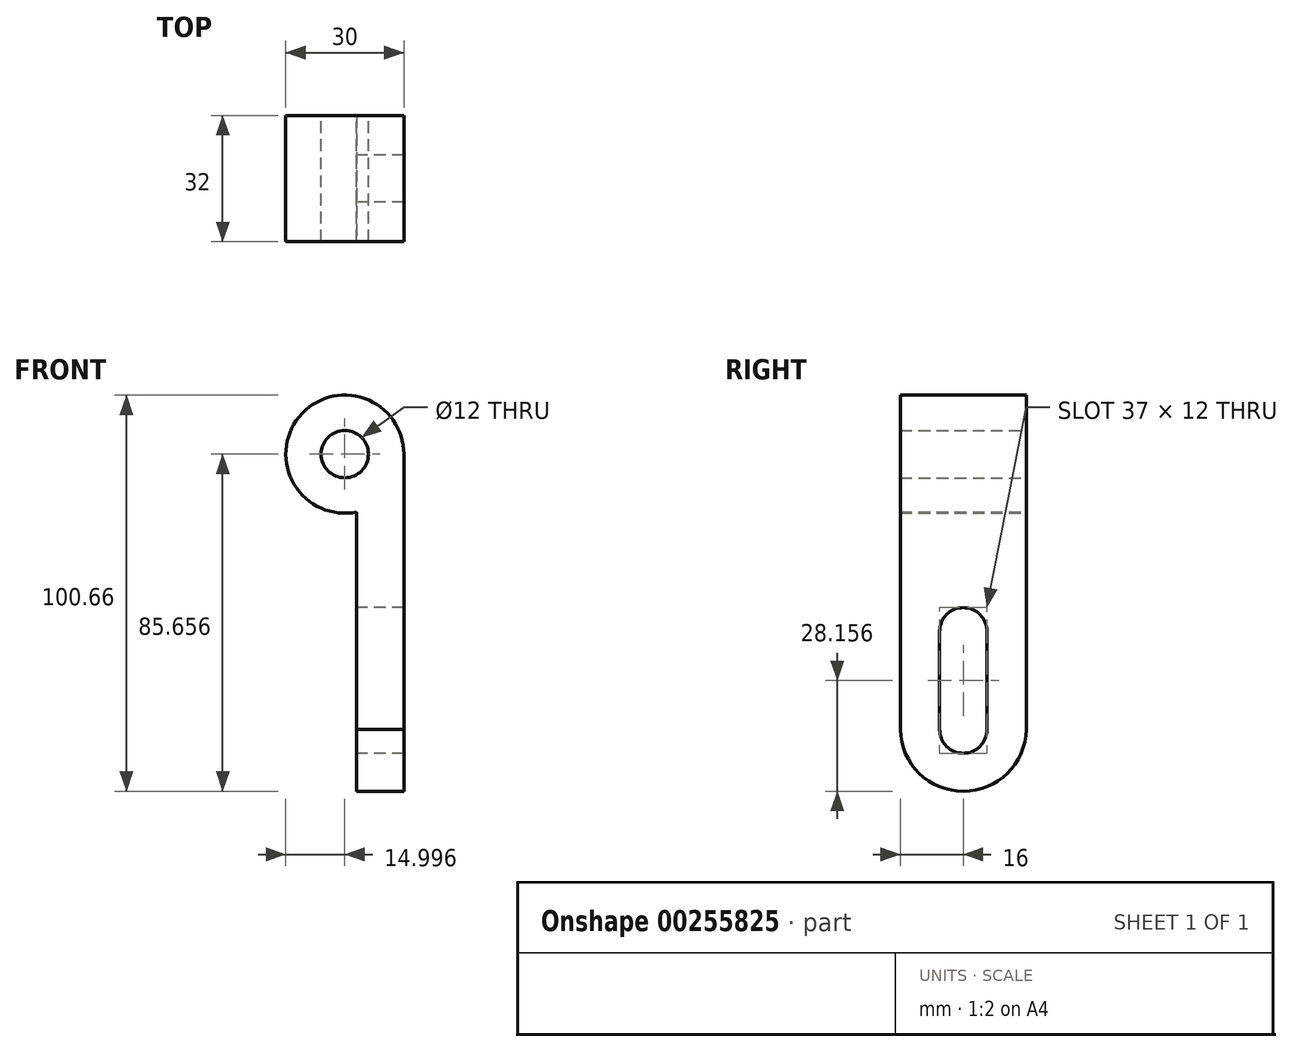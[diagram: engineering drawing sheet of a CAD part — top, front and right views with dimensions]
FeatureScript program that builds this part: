
annotation { "Feature Type Name" : "Feature", "Feature Type Description" : "" }
export const myFeature = defineFeature(function(context is Context, id is Id, definition is map)
    precondition{}
    {
        {
            var Q0;
            Q0=qCreatedBy(makeId("Front.planeOp"),FACE);
            var sketch = newSketch(context, id + "F0", { "sketchPlane" : qUnion([Q0])});
            skArc(sketch, "E0", {"start": v(2.19, -13.8) * mm, "mid": v(-24.43, -4.32) * mm, "end": v(-9.81, -28.5) * mm});
            skCircle(sketch, "E1", {"center": v(-12.81, -13.8) * mm, "radius": 6 * mm});
            skLineSegment(sketch, "E2", {"start": v(2.19, -13.8) * mm, "end": v(2.19, -99.8) * mm});
            skLineSegment(sketch, "E3", {"start": v(2.19, -99.8) * mm, "end": v(-9.81, -99.8) * mm});
            skLineSegment(sketch, "E4", {"start": v(-9.81, -99.8) * mm, "end": v(-9.81, -28.5) * mm});
            skSolve(sketch);
        }
        {
            var Q0;
            Q0=makeQuery(id+"F0.imprint","IMPRINT",FACE,{"disambiguationData":[TD([[makeQuery(id+"F0.imprint","IMPRINT",EDGE,{"derivedFrom":sQuery(id+"F0.wireOp",EDGE,"E0")}),1.0]])]});
            extrude(context, id + "F1", {"entities" : qUnion([Q0]), "endBound" : BoundingType.SYMMETRIC, "depth" : 32 * mm});
        }
        {
            var Q0;
            Q0=qCreatedBy(makeId("Right.planeOp"),FACE);
            cPlane(context, id + "F2", {"entities" : qUnion([Q0]), "cplaneType" : CPlaneType.OFFSET, "offset" : 30 * mm, "oppositeDirection" : true, "width" : 150 * mm, "height" : 150 * mm});
        }
        {
            var Q0;
            Q0=qCreatedBy(id+"F2.planeOp",FACE);
            var sketch = newSketch(context, id + "F3", { "sketchPlane" : qUnion([Q0])});
            skLineSegment(sketch, "E5", {"start": v(-16, 1.2) * mm, "end": v(16, 1.2) * mm});
            skLineSegment(sketch, "E6.0", {"start": v(-16, -13.8) * mm, "end": v(-16, -99.8) * mm});
            skLineSegment(sketch, "E7.0", {"start": v(16, -99.8) * mm, "end": v(16, -28.5) * mm});
            skLineSegment(sketch, "E8.0", {"start": v(-16, -99.8) * mm, "end": v(16, -99.8) * mm});
            skLineSegment(sketch, "E9.bottom", {"start": v(6, 1.2) * mm, "end": v(-6, 1.2) * mm});
            skLineSegment(sketch, "E9.top", {"start": v(6, -38.8) * mm, "end": v(-6, -38.8) * mm});
            skLineSegment(sketch, "E9.left", {"start": v(6, 1.2) * mm, "end": v(6, -38.8) * mm});
            skLineSegment(sketch, "E9.right", {"start": v(-6, 1.2) * mm, "end": v(-6, -38.8) * mm});
            skLineSegment(sketch, "E10.bottom", {"start": v(6, -58.8) * mm, "end": v(-6, -58.8) * mm});
            skLineSegment(sketch, "E10.top", {"start": v(6, -83.8) * mm, "end": v(-6, -83.8) * mm});
            skLineSegment(sketch, "E10.left", {"start": v(6, -58.8) * mm, "end": v(6, -83.8) * mm});
            skLineSegment(sketch, "E10.right", {"start": v(-6, -58.8) * mm, "end": v(-6, -83.8) * mm});
            skArc(sketch, "E11", {"start": v(-16, -83.8) * mm, "mid": v(0, -99.46) * mm, "end": v(16, -83.8) * mm});
            skArc(sketch, "E12", {"start": v(-6, -83.8) * mm, "mid": v(0, -89.8) * mm, "end": v(6, -83.8) * mm});
            skArc(sketch, "E13", {"start": v(6, -58.8) * mm, "mid": v(0, -52.8) * mm, "end": v(-6, -58.8) * mm});
            skSolve(sketch);
        }
        {
            var Q0;
            {var subQ0=sQuery(id+"F3.wireOp",EDGE,"E8.0");Q0=makeQuery(id+"F3.imprint","IMPRINT",FACE,{"disambiguationData":[TD([[makeQuery(id+"F3.imprint","IMPRINT",EDGE,{"derivedFrom":subQ0}),1.0]])]});}
            var Q1;
            Q1=makeQuery(id+"F3.imprint","IMPRINT",FACE,{"disambiguationData":[TD([[makeQuery(id+"F3.imprint","IMPRINT",EDGE,{"derivedFrom":sQuery(id+"F3.wireOp",EDGE,"E10.bottom")}),-1.0]])]});
            var Q2;
            Q2=makeQuery(id+"F3.imprint","IMPRINT",FACE,{"disambiguationData":[TD([[makeQuery(id+"F3.imprint","IMPRINT",EDGE,{"derivedFrom":sQuery(id+"F3.wireOp",EDGE,"E10.top")}),1.0]])]});
            var Q3;
            Q3=makeQuery(id+"F3.imprint","IMPRINT",FACE,{"disambiguationData":[TD([[makeQuery(id+"F3.imprint","IMPRINT",EDGE,{"derivedFrom":sQuery(id+"F3.wireOp",EDGE,"E10.bottom")}),1.0]])]});
            var Q4;
            {var subQ0=sQuery(id+"F3.wireOp",EDGE,"E8.0");Q4=makeQuery(id+"F3.imprint","IMPRINT",FACE,{"disambiguationData":[TD([[makeQuery(id+"F3.imprint","IMPRINT",EDGE,{"derivedFrom":subQ0}),1.0]])]});}
            var Q5;
            Q5=makeQuery(id+"F3.imprint","IMPRINT",FACE,{"disambiguationData":[TD([[makeQuery(id+"F3.imprint","IMPRINT",EDGE,{"derivedFrom":sQuery(id+"F3.wireOp",EDGE,"E10.bottom")}),-1.0]])]});
            var Q6;
            Q6=makeQuery(id+"F3.imprint","IMPRINT",FACE,{"disambiguationData":[TD([[makeQuery(id+"F3.imprint","IMPRINT",EDGE,{"derivedFrom":sQuery(id+"F3.wireOp",EDGE,"E10.top")}),1.0]])]});
            var Q7;
            Q7=makeQuery(id+"F3.imprint","IMPRINT",FACE,{"disambiguationData":[TD([[makeQuery(id+"F3.imprint","IMPRINT",EDGE,{"derivedFrom":sQuery(id+"F3.wireOp",EDGE,"E10.bottom")}),1.0]])]});
            var Q8;
            Q8=makeQuery(id+"F3.imprint","IMPRINT",FACE,{"disambiguationData":[TD([[makeQuery(id+"F3.imprint","IMPRINT",EDGE,{"derivedFrom":sQuery(id+"F3.wireOp",EDGE,"E9.bottom")}),1.0]])]});
            extrude(context, id + "F4", {"entities" : qUnion([Q0, Q1, Q2, Q3, Q4, Q5, Q6, Q7, Q8]), "operationType" : NewBodyOperationType.REMOVE, "endBound" : BoundingType.THROUGH_ALL, "depth" : 25 * mm});
        }
    });
